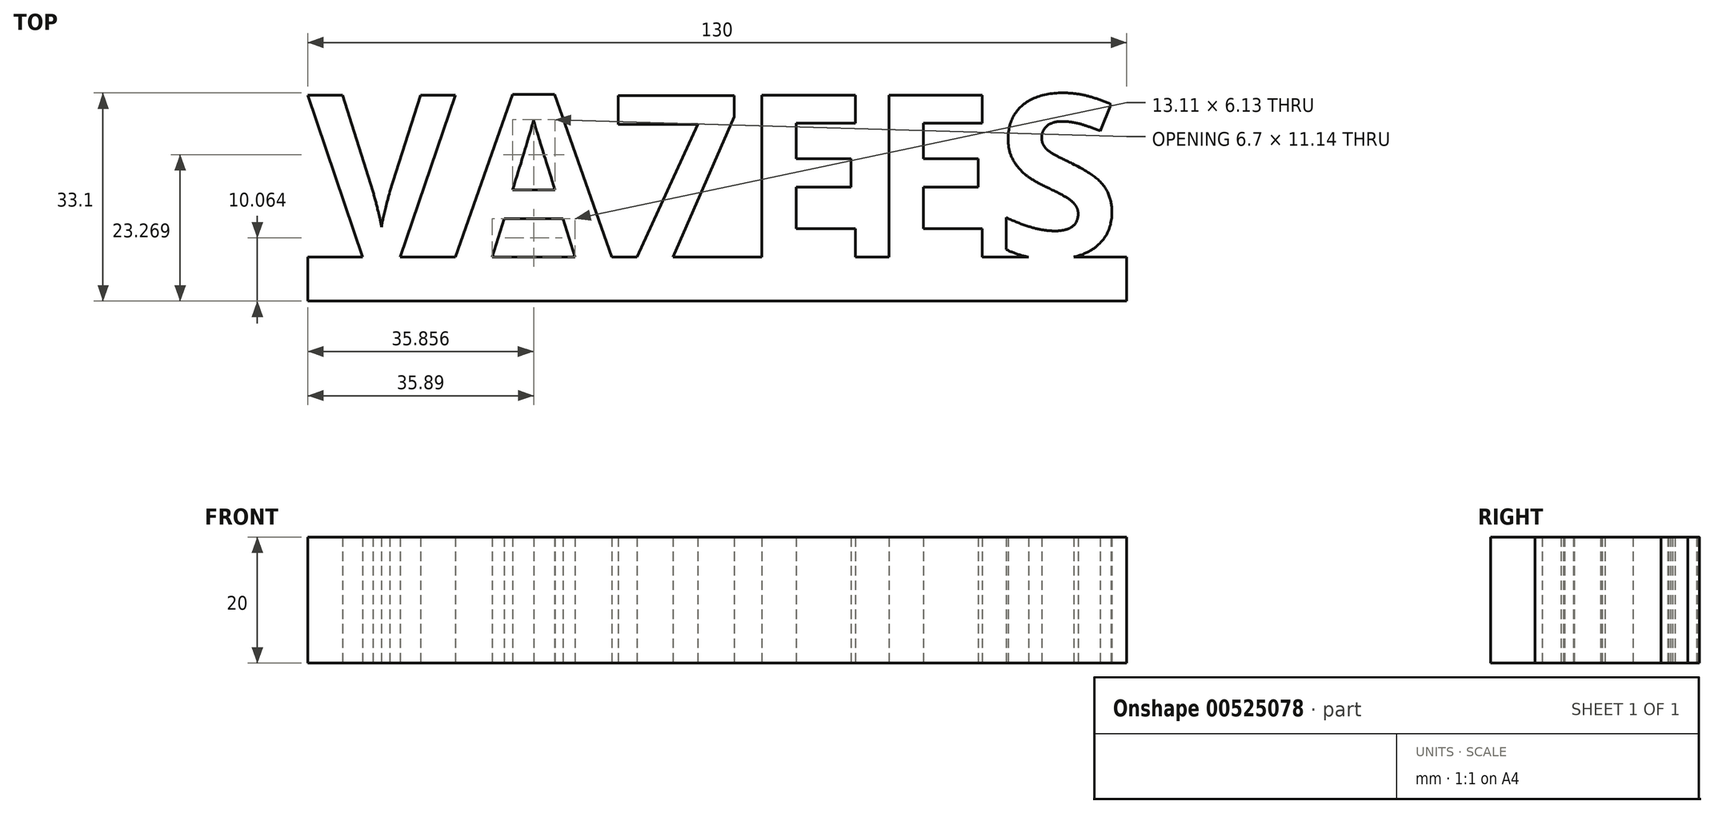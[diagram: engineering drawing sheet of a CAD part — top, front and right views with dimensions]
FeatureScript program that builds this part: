
annotation { "Feature Type Name" : "Feature", "Feature Type Description" : "" }
export const myFeature = defineFeature(function(context is Context, id is Id, definition is map)
    precondition{}
    {
        {
            var Q0;
            Q0=qCreatedBy(makeId("Top.planeOp"),FACE);
            var sketch = newSketch(context, id + "F0", { "sketchPlane" : qUnion([Q0])});
            skText(sketch, "E0", { "text": "VA7EES", "fontName": "OpenSans-Bold.ttf"});
            skLineSegment(sketch, "E1.bottom", {"start": v(-65, 0) * mm, "end": v(65, 0) * mm});
            skLineSegment(sketch, "E1.top", {"start": v(-65, -7) * mm, "end": v(65, -7) * mm});
            skLineSegment(sketch, "E1.left", {"start": v(-65, 0) * mm, "end": v(-65, -7) * mm});
            skLineSegment(sketch, "E1.right", {"start": v(65, 0) * mm, "end": v(65, -7) * mm});
            const initialGuessF0  = {"E0": [-0.065, 0, 1, 0, 0.02595]};
            skSetInitialGuess(sketch, initialGuessF0);
            skSolve(sketch);
        }
        {
            var Q0;
            Q0 = qSketchRegion(id + "F0", true);
            extrude(context, id + "F1", {"entities" : qUnion([Q0]), "depth" : 20 * mm, "offsetDistance" : 25 * mm});
        }
    });
